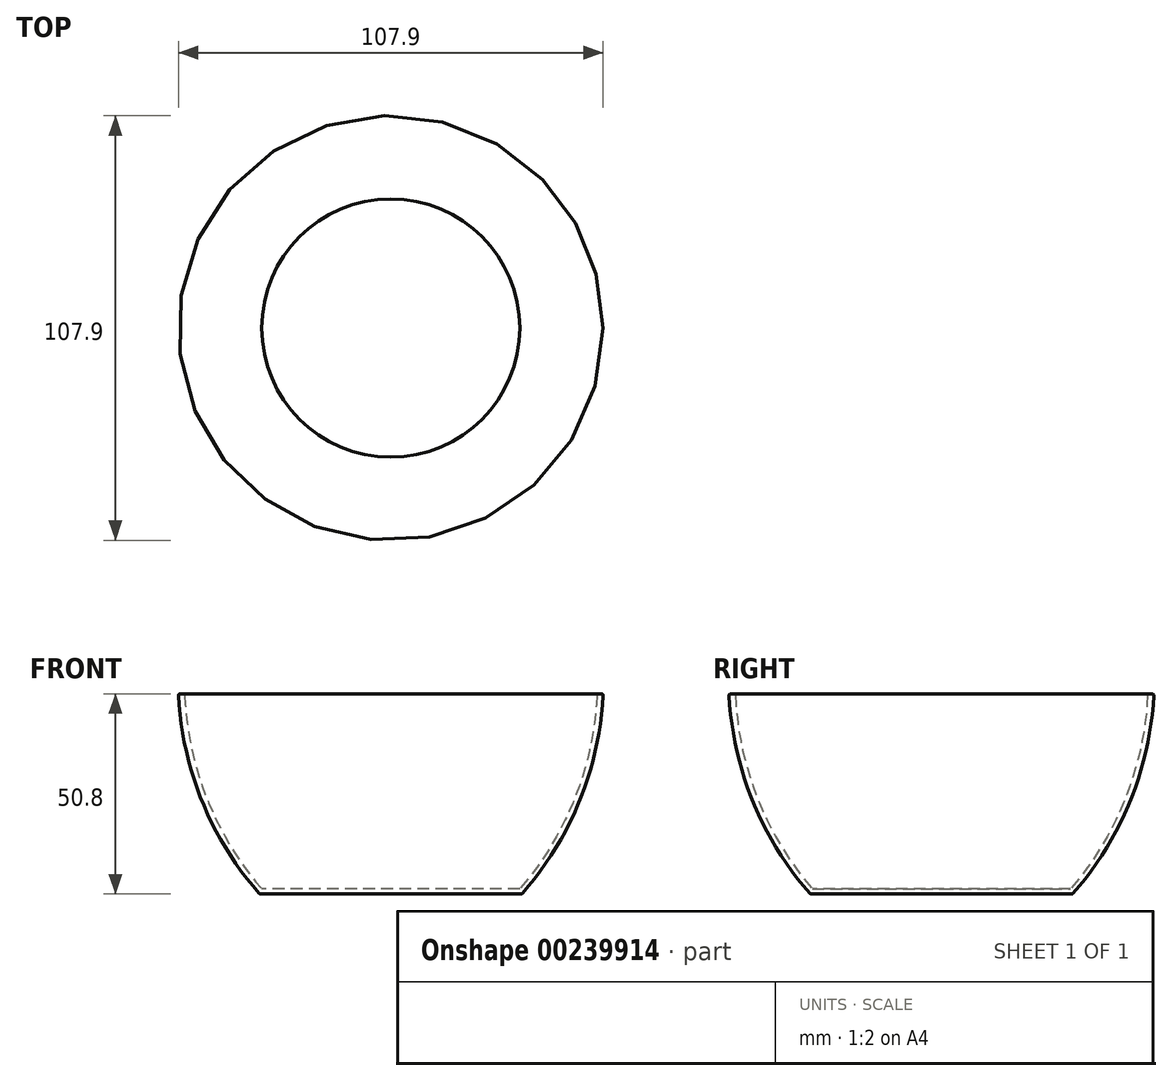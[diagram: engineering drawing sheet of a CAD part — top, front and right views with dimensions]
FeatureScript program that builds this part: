
annotation { "Feature Type Name" : "Feature", "Feature Type Description" : "" }
export const myFeature = defineFeature(function(context is Context, id is Id, definition is map)
    precondition{}
    {
        {
            var Q0;
            Q0=qCreatedBy(makeId("Front.planeOp"),FACE);
            var sketch = newSketch(context, id + "F0", { "sketchPlane" : qUnion([Q0])});
            skLineSegment(sketch, "E0", {"start": v(0, 0) * mm, "end": v(0, -50.8) * mm});
            skLineSegment(sketch, "E1", {"start": v(0, -50.8) * mm, "end": v(33.34, -50.8) * mm});
            skLineSegment(sketch, "E2", {"start": v(0, 0) * mm, "end": v(53.98, 0) * mm});
            skArc(sketch, "E3", {"start": v(33.34, -50.8) * mm, "mid": v(47.98, -27.16) * mm, "end": v(53.97, 0) * mm});
            skPoint(sketch, "E4", {"position": v(52.39, 0) * mm});
            skPoint(sketch, "E5", {"position": v(34.38, -49.6) * mm});
            skPoint(sketch, "E6", {"position": v(32.79, -49.6) * mm});
            skArc(sketch, "E7", {"start": v(32.79, -49.6) * mm, "mid": v(46.75, -26.45) * mm, "end": v(52.39, 0) * mm});
            skLineSegment(sketch, "E8", {"start": v(32.79, -49.6) * mm, "end": v(0, -49.6) * mm});
            skSolve(sketch);
        }
        {
            var Q0;
            {var subQ3=sQuery(id+"F0.wireOp",EDGE,"E1");Q0=makeQuery(id+"F0.imprint","IMPRINT",FACE,{"disambiguationData":[TD([[makeQuery(id+"F0.imprint","IMPRINT",EDGE,{"derivedFrom":subQ3}),1.0]])]});}
            var Q1;
            Q1=sQuery(id+"F0.wireOp",EDGE,"E0");
            revolve(context, id + "F1", {"entities" : qUnion([Q0]), "axis" : qUnion([Q1]), "revolveType" : RevolveType.FULL});
        }
        {
            var Q0;
            Q0=makeQuery(id+"F1.opRevolve","SWEPT_EDGE",EDGE,{"disambiguationData":[OSD([sQuery(id+"F0.wireOp",EDGE,"E2"),sQuery(id+"F0.wireOp",EDGE,"E3")])]});
            fillet(context, id + "F2", {"entities" : qUnion([Q0]), "radius" : 0.4 * mm, "tangentPropagation" : true, "allowEdgeOverflow" : false});
        }
        {
            var Q0;
            Q0=makeQuery(id+"F1.opRevolve","SWEPT_EDGE",EDGE,{"disambiguationData":[OSD([sQuery(id+"F0.wireOp",EDGE,"E2"),sQuery(id+"F0.wireOp",EDGE,"E7")])]});
            fillet(context, id + "F3", {"entities" : qUnion([Q0]), "radius" : 0.4 * mm, "tangentPropagation" : true, "allowEdgeOverflow" : false});
        }
        {
            var Q0;
            Q0=makeQuery(id+"F1.opRevolve","SWEPT_EDGE",EDGE,{"disambiguationData":[OSD([sQuery(id+"F0.wireOp",EDGE,"E1"),sQuery(id+"F0.wireOp",EDGE,"E3")])]});
            fillet(context, id + "F4", {"entities" : qUnion([Q0]), "radius" : 0.4 * mm, "tangentPropagation" : true, "allowEdgeOverflow" : false});
        }
    });
